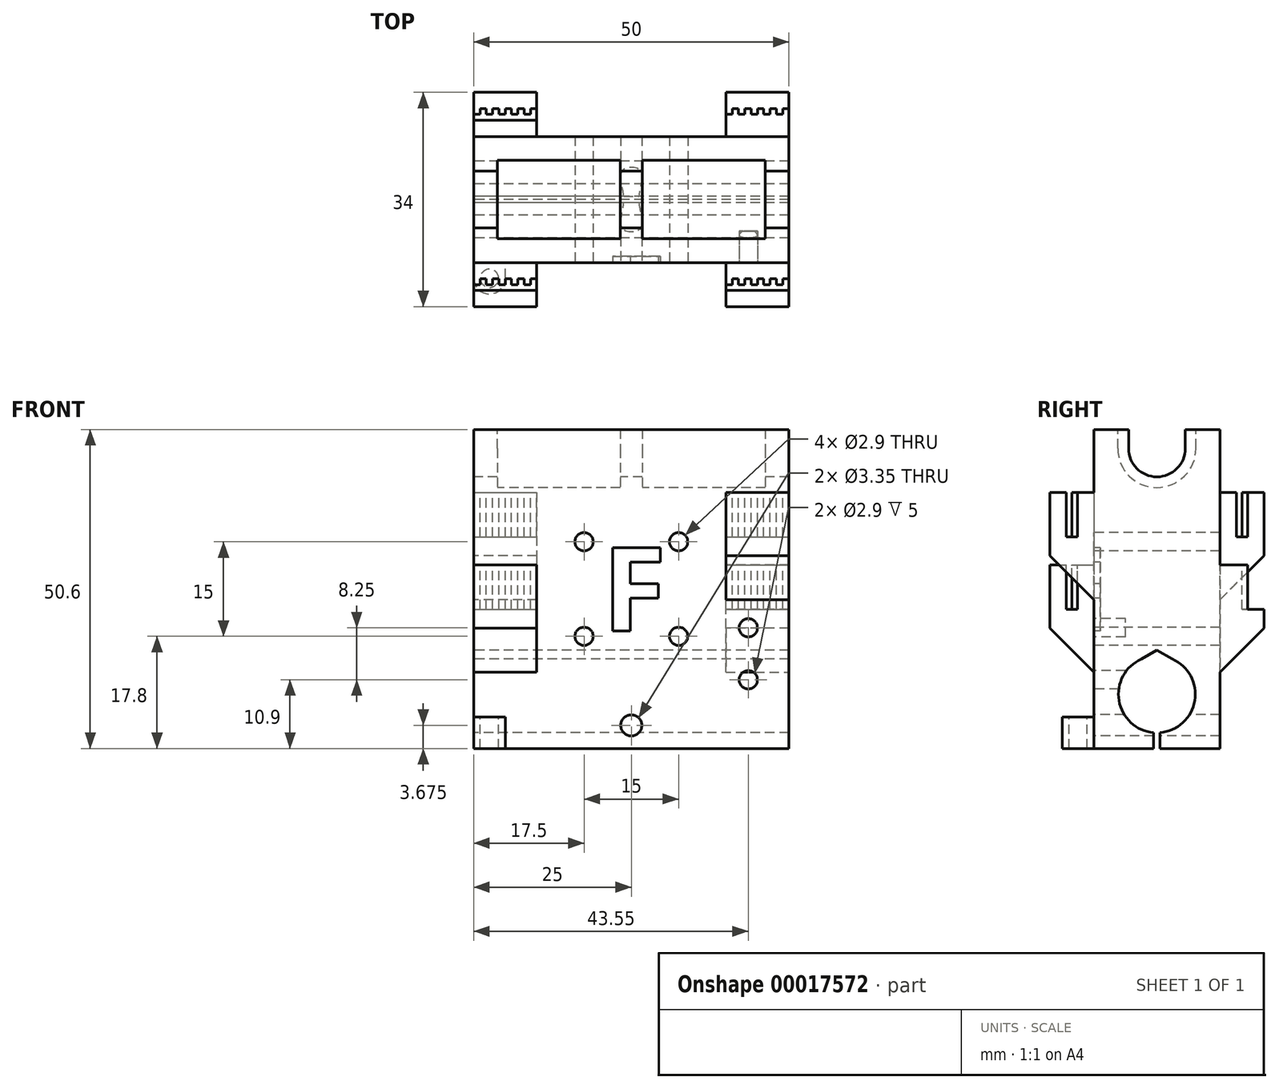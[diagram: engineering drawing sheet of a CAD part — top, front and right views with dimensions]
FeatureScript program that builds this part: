
annotation { "Feature Type Name" : "Feature", "Feature Type Description" : "" }
export const myFeature = defineFeature(function(context is Context, id is Id, definition is map)
    precondition{}
    {
        {
            var Q0;
            Q0=qCreatedBy(makeId("Top.planeOp"),FACE);
            var sketch = newSketch(context, id + "F0", { "sketchPlane" : qUnion([Q0])});
            skLineSegment(sketch, "E0.bottom", {"start": v(0, 0) * mm, "end": v(50, 0) * mm});
            skLineSegment(sketch, "E0.top", {"start": v(0, 20) * mm, "end": v(50, 20) * mm});
            skLineSegment(sketch, "E0.left", {"start": v(0, 0) * mm, "end": v(0, 20) * mm});
            skLineSegment(sketch, "E0.right", {"start": v(50, 0) * mm, "end": v(50, 20) * mm});
            skSolve(sketch);
        }
        {
            var Q0;
            Q0=qSketchRegion(id+"F0",true);
            extrude(context, id + "F1", {"entities" : qUnion([Q0]), "depth" : 50.6 * mm});
        }
        {
            var Q0;
            Q0=makeQuery(id+"F1.opExtrude","SWEPT_FACE",FACE,{"disambiguationData":[OSD([sQuery(id+"F0.wireOp",EDGE,"E0.left")])]});
            var sketch = newSketch(context, id + "F2", { "sketchPlane" : qUnion([Q0])});
            skCircle(sketch, "E1", {"center": v(-10, 8.6) * mm, "radius": 6.1 * mm});
            skCircle(sketch, "E2", {"center": v(-10, 47.6) * mm, "radius": 4.5 * mm});
            skLineSegment(sketch, "E3", {"start": v(-20, 47.6) * mm, "end": v(0, 47.6) * mm, "construction": true});
            skLineSegment(sketch, "E4", {"start": v(-14.5, 50.6) * mm, "end": v(-14.5, 47.6) * mm});
            skLineSegment(sketch, "E5", {"start": v(-5.5, 50.6) * mm, "end": v(-5.5, 47.6) * mm});
            skLineSegment(sketch, "E6", {"start": v(-20, 8.6) * mm, "end": v(0, 8.6) * mm, "construction": true});
            skLineSegment(sketch, "E7", {"start": v(-10, 8.6) * mm, "end": v(-10, 0) * mm, "construction": true});
            skLineSegment(sketch, "E8", {"start": v(-10, 0) * mm, "end": v(-10.5, 0) * mm});
            skLineSegment(sketch, "E9", {"start": v(-10.5, 0) * mm, "end": v(-10.5, 2.52) * mm});
            skLineSegment(sketch, "E10", {"start": v(-10.5, 2.52) * mm, "end": v(-9.5, 2.52) * mm});
            skLineSegment(sketch, "E11", {"start": v(-9.5, 2.52) * mm, "end": v(-9.5, 0) * mm});
            skLineSegment(sketch, "E12", {"start": v(-9.5, 0) * mm, "end": v(-10, 0) * mm});
            skLineSegment(sketch, "E13", {"start": v(-10, 14.7) * mm, "end": v(-10, 15.6) * mm});
            skLineSegment(sketch, "E14", {"start": v(-10, 15.6) * mm, "end": v(-6.39, 13.51) * mm});
            skLineSegment(sketch, "E15", {"start": v(-10, 15.6) * mm, "end": v(-13.61, 13.51) * mm});
            skCircle(sketch, "E16", {"center": v(-10, 47.6) * mm, "radius": 6.2 * mm});
            skLineSegment(sketch, "E17", {"start": v(-3.8, 47.6) * mm, "end": v(-3.8, 50.6) * mm});
            skLineSegment(sketch, "E18", {"start": v(-16.2, 47.6) * mm, "end": v(-16.2, 50.6) * mm});
            skSolve(sketch);
        }
        {
            var Q0;
            {var subQ0=sQuery(id+"F2.wireOp",EDGE,"E14");var subQ1=sQuery(id+"F2.wireOp",EDGE,"E1");var subQ3=makeQuery(id+"F2.imprint","INTERSECT",VERTEX,{"disambiguationData":[OD(0.0)],"derivedFrom":[subQ1,subQ0]});Q0=makeQuery(id+"F2.imprint","IMPRINT",FACE,{"disambiguationData":[TD([[makeQuery(id+"F2.imprint","IMPRINT",EDGE,{"disambiguationData":[TD([[subQ3,-1.0]])],"derivedFrom":subQ1}),1.0]])]});}
            var Q1;
            {var subQ0=sQuery(id+"F2.wireOp",EDGE,"E15");var subQ1=sQuery(id+"F2.wireOp",EDGE,"E1");var subQ3=makeQuery(id+"F2.imprint","INTERSECT",VERTEX,{"disambiguationData":[OD(0.0)],"derivedFrom":[subQ1,subQ0]});Q1=makeQuery(id+"F2.imprint","IMPRINT",FACE,{"disambiguationData":[TD([[makeQuery(id+"F2.imprint","IMPRINT",EDGE,{"disambiguationData":[TD([[subQ3,1.0]])],"derivedFrom":subQ1}),1.0]])]});}
            var Q2;
            Q2=makeQuery(id+"F2.imprint","IMPRINT",FACE,{"disambiguationData":[TD([[makeQuery(id+"F2.imprint","IMPRINT",EDGE,{"derivedFrom":sQuery(id+"F2.wireOp",EDGE,"E8")}),-1.0]])]});
            var Q3;
            {var subQ0=sQuery(id+"F2.wireOp",EDGE,"E10");Q3=makeQuery(id+"F2.imprint","IMPRINT",FACE,{"disambiguationData":[TD([[makeQuery(id+"F2.imprint","IMPRINT",EDGE,{"derivedFrom":subQ0}),-1.0]])]});}
            var Q4;
            {var subQ3=sQuery(id+"F2.wireOp",EDGE,"E13");Q4=makeQuery(id+"F2.imprint","IMPRINT",FACE,{"disambiguationData":[TD([[makeQuery(id+"F2.imprint","IMPRINT",EDGE,{"derivedFrom":subQ3}),-1.0]])]});}
            var Q5;
            {var subQ3=sQuery(id+"F2.wireOp",EDGE,"E13");Q5=makeQuery(id+"F2.imprint","IMPRINT",FACE,{"disambiguationData":[TD([[makeQuery(id+"F2.imprint","IMPRINT",EDGE,{"derivedFrom":subQ3}),1.0]])]});}
            var Q6;
            {var subQ7=sQuery(id+"F2.wireOp",EDGE,"E10");Q6=makeQuery(id+"F2.imprint","IMPRINT",FACE,{"disambiguationData":[TD([[makeQuery(id+"F2.imprint","IMPRINT",EDGE,{"derivedFrom":subQ7}),1.0]])]});}
            var Q7;
            {var subQ3=sQuery(id+"F2.wireOp",EDGE,"E5");Q7=makeQuery(id+"F2.imprint","IMPRINT",FACE,{"disambiguationData":[TD([[makeQuery(id+"F2.imprint","IMPRINT",EDGE,{"derivedFrom":subQ3}),-1.0]])]});}
            var Q8;
            {var subQ0=sQuery(id+"F2.wireOp",EDGE,"E4");Q8=makeQuery(id+"F2.imprint","IMPRINT",FACE,{"disambiguationData":[TD([[makeQuery(id+"F2.imprint","IMPRINT",EDGE,{"derivedFrom":subQ0}),1.0]])]});}
            var Q9;
            {var subQ0=sQuery(id+"F2.wireOp",EDGE,"E4");Q9=makeQuery(id+"F2.imprint","IMPRINT",FACE,{"disambiguationData":[TD([[makeQuery(id+"F2.imprint","IMPRINT",EDGE,{"derivedFrom":subQ0}),1.0]])]});}
            var Q10;
            {var subQ3=sQuery(id+"F2.wireOp",EDGE,"E5");Q10=makeQuery(id+"F2.imprint","IMPRINT",FACE,{"disambiguationData":[TD([[makeQuery(id+"F2.imprint","IMPRINT",EDGE,{"derivedFrom":subQ3}),-1.0]])]});}
            var Q11;
            {var subQ1=sQuery(id+"F2.wireOp",EDGE,"E2");var subQ4=makeQuery(id+"F2.imprint","INTERSECT",VERTEX,{"derivedFrom":[subQ1,sQuery(id+"F2.wireOp",EDGE,"E5")]});Q11=makeQuery(id+"F2.imprint","IMPRINT",FACE,{"disambiguationData":[TD([[makeQuery(id+"F2.imprint","IMPRINT",EDGE,{"disambiguationData":[TD([[subQ4,-1.0]])],"derivedFrom":subQ1}),1.0]])]});}
            extrude(context, id + "F3", {"entities" : qUnion([Q0, Q1, Q2, Q3, Q4, Q5, Q6, Q7, Q8, Q9, Q10, Q11]), "operationType" : NewBodyOperationType.REMOVE, "endBound" : BoundingType.THROUGH_ALL, "oppositeDirection" : true, "depth" : 25 * mm});
        }
        {
            var Q0;
            {var subQ3=sQuery(id+"F2.wireOp",EDGE,"E4");Q0=makeQuery(id+"F2.imprint","IMPRINT",FACE,{"disambiguationData":[TD([[makeQuery(id+"F2.imprint","IMPRINT",EDGE,{"derivedFrom":subQ3}),-1.0]])]});}
            var Q1;
            {var subQ3=sQuery(id+"F2.wireOp",EDGE,"E18");Q1=makeQuery(id+"F2.imprint","IMPRINT",FACE,{"disambiguationData":[TD([[makeQuery(id+"F2.imprint","IMPRINT",EDGE,{"derivedFrom":subQ3}),-1.0]])]});}
            var Q2;
            {var subQ3=sQuery(id+"F2.wireOp",EDGE,"E17");Q2=makeQuery(id+"F2.imprint","IMPRINT",FACE,{"disambiguationData":[TD([[makeQuery(id+"F2.imprint","IMPRINT",EDGE,{"derivedFrom":subQ3}),1.0]])]});}
            extrude(context, id + "F4", {"entities" : qUnion([Q0, Q1, Q2]), "operationType" : NewBodyOperationType.REMOVE, "oppositeDirection" : true, "depth" : 46.25 * mm});
        }
        {
            var Q0;
            {var subQ3=sQuery(id+"F2.wireOp",EDGE,"E4");Q0=makeQuery(id+"F2.imprint","IMPRINT",FACE,{"disambiguationData":[TD([[makeQuery(id+"F2.imprint","IMPRINT",EDGE,{"derivedFrom":subQ3}),-1.0]])]});}
            var Q1;
            {var subQ3=sQuery(id+"F2.wireOp",EDGE,"E18");Q1=makeQuery(id+"F2.imprint","IMPRINT",FACE,{"disambiguationData":[TD([[makeQuery(id+"F2.imprint","IMPRINT",EDGE,{"derivedFrom":subQ3}),-1.0]])]});}
            var Q2;
            {var subQ3=sQuery(id+"F2.wireOp",EDGE,"E17");Q2=makeQuery(id+"F2.imprint","IMPRINT",FACE,{"disambiguationData":[TD([[makeQuery(id+"F2.imprint","IMPRINT",EDGE,{"derivedFrom":subQ3}),1.0]])]});}
            extrude(context, id + "F5", {"entities" : qUnion([Q0, Q1, Q2]), "operationType" : NewBodyOperationType.ADD, "oppositeDirection" : true, "depth" : 26.75 * mm});
        }
        {
            var Q0;
            {var subQ3=sQuery(id+"F2.wireOp",EDGE,"E4");Q0=makeQuery(id+"F2.imprint","IMPRINT",FACE,{"disambiguationData":[TD([[makeQuery(id+"F2.imprint","IMPRINT",EDGE,{"derivedFrom":subQ3}),-1.0]])]});}
            var Q1;
            {var subQ3=sQuery(id+"F2.wireOp",EDGE,"E18");Q1=makeQuery(id+"F2.imprint","IMPRINT",FACE,{"disambiguationData":[TD([[makeQuery(id+"F2.imprint","IMPRINT",EDGE,{"derivedFrom":subQ3}),-1.0]])]});}
            var Q2;
            {var subQ3=sQuery(id+"F2.wireOp",EDGE,"E17");Q2=makeQuery(id+"F2.imprint","IMPRINT",FACE,{"disambiguationData":[TD([[makeQuery(id+"F2.imprint","IMPRINT",EDGE,{"derivedFrom":subQ3}),1.0]])]});}
            extrude(context, id + "F6", {"entities" : qUnion([Q0, Q1, Q2]), "operationType" : NewBodyOperationType.REMOVE, "oppositeDirection" : true, "depth" : 23.25 * mm});
        }
        {
            var Q0;
            {var subQ3=sQuery(id+"F2.wireOp",EDGE,"E4");Q0=makeQuery(id+"F2.imprint","IMPRINT",FACE,{"disambiguationData":[TD([[makeQuery(id+"F2.imprint","IMPRINT",EDGE,{"derivedFrom":subQ3}),-1.0]])]});}
            var Q1;
            {var subQ3=sQuery(id+"F2.wireOp",EDGE,"E18");Q1=makeQuery(id+"F2.imprint","IMPRINT",FACE,{"disambiguationData":[TD([[makeQuery(id+"F2.imprint","IMPRINT",EDGE,{"derivedFrom":subQ3}),-1.0]])]});}
            var Q2;
            {var subQ3=sQuery(id+"F2.wireOp",EDGE,"E17");Q2=makeQuery(id+"F2.imprint","IMPRINT",FACE,{"disambiguationData":[TD([[makeQuery(id+"F2.imprint","IMPRINT",EDGE,{"derivedFrom":subQ3}),1.0]])]});}
            extrude(context, id + "F7", {"entities" : qUnion([Q0, Q1, Q2]), "operationType" : NewBodyOperationType.ADD, "oppositeDirection" : true, "depth" : 3.75 * mm});
        }
        {
            var Q0;
            Q0=makeQuery(id+"F1.opExtrude","SWEPT_FACE",FACE,{"disambiguationData":[OSD([sQuery(id+"F0.wireOp",EDGE,"E0.bottom")])]});
            var sketch = newSketch(context, id + "F8", { "sketchPlane" : qUnion([Q0])});
            skLineSegment(sketch, "E19.bottom", {"start": v(0, 29.1) * mm, "end": v(10, 29.1) * mm});
            skLineSegment(sketch, "E19.top", {"start": v(0, 9.1) * mm, "end": v(10, 9.1) * mm});
            skLineSegment(sketch, "E19.left", {"start": v(0, 29.1) * mm, "end": v(0, 9.1) * mm});
            skLineSegment(sketch, "E19.right", {"start": v(10, 29.1) * mm, "end": v(10, 9.1) * mm});
            skLineSegment(sketch, "E20.bottom", {"start": v(50, 40.6) * mm, "end": v(40, 40.6) * mm});
            skLineSegment(sketch, "E20.top", {"start": v(50, 20.6) * mm, "end": v(40, 20.6) * mm});
            skLineSegment(sketch, "E20.left", {"start": v(50, 40.6) * mm, "end": v(50, 20.6) * mm});
            skLineSegment(sketch, "E20.right", {"start": v(40, 40.6) * mm, "end": v(40, 20.6) * mm});
            skPoint(sketch, "E21", {"position": v(0, 47.6) * mm});
            skPoint(sketch, "E22", {"position": v(0, 8.6) * mm});
            skSolve(sketch);
        }
        {
            var Q0;
            Q0=qSketchRegion(id+"F8",true);
            extrude(context, id + "F9", {"entities" : qUnion([Q0]), "operationType" : NewBodyOperationType.ADD, "depth" : 7 * mm});
        }
        {
            var Q0;
            Q0=makeQuery(id+"F9.opExtrude","CAP_EDGE",EDGE,{"disambiguationData":[OSD([sQuery(id+"F8.wireOp",EDGE,"E19.top")])],"isStart":false});
            var Q1;
            Q1=makeQuery(id+"F9.opExtrude","CAP_EDGE",EDGE,{"disambiguationData":[OSD([sQuery(id+"F8.wireOp",EDGE,"E20.top")])],"isStart":false});
            chamfer(context, id + "F10", {"entities" : qUnion([Q0, Q1]), "width" : 10 * mm, "tangentPropagation" : true});
        }
        {
            var Q0;
            Q0=makeQuery(id+"F9.opExtrude","SWEPT_FACE",FACE,{"disambiguationData":[OSD([sQuery(id+"F8.wireOp",EDGE,"E19.bottom")])]});
            var sketch = newSketch(context, id + "F11", { "sketchPlane" : qUnion([Q0])});
            skLineSegment(sketch, "E23", {"start": v(-935.9, 0) * mm, "end": v(-935.88, -4.54) * mm});
            skLineSegment(sketch, "E24.left", {"start": v(0, -4.4) * mm, "end": v(0, -2.6) * mm});
            skLineSegment(sketch, "E25", {"start": v(6, -3.5) * mm, "end": v(7, -3.5) * mm});
            skLineSegment(sketch, "E26", {"start": v(4, -3.5) * mm, "end": v(5, -3.5) * mm});
            skLineSegment(sketch, "E27", {"start": v(0, -3.5) * mm, "end": v(1, -3.5) * mm});
            skLineSegment(sketch, "E28", {"start": v(7, -2.6) * mm, "end": v(8, -2.6) * mm});
            skLineSegment(sketch, "E29", {"start": v(2, -3.5) * mm, "end": v(3, -3.5) * mm});
            skLineSegment(sketch, "E30", {"start": v(3, -2.6) * mm, "end": v(4, -2.6) * mm});
            skLineSegment(sketch, "E31", {"start": v(8, -3.5) * mm, "end": v(9, -3.5) * mm});
            skLineSegment(sketch, "E32", {"start": v(8, -2.6) * mm, "end": v(8, -3.5) * mm});
            skLineSegment(sketch, "E33", {"start": v(9, -3.5) * mm, "end": v(9, -2.6) * mm});
            skLineSegment(sketch, "E34", {"start": v(10, -2.6) * mm, "end": v(10, -3.5) * mm});
            skLineSegment(sketch, "E35", {"start": v(6, -2.6) * mm, "end": v(6, -3.5) * mm});
            skLineSegment(sketch, "E36", {"start": v(2, -2.6) * mm, "end": v(2, -3.5) * mm});
            skLineSegment(sketch, "E37", {"start": v(1, -2.6) * mm, "end": v(2, -2.6) * mm});
            skLineSegment(sketch, "E38", {"start": v(1, -3.5) * mm, "end": v(1, -2.6) * mm});
            skLineSegment(sketch, "E39", {"start": v(9, -2.6) * mm, "end": v(10, -2.6) * mm});
            skLineSegment(sketch, "E40", {"start": v(5, -2.6) * mm, "end": v(6, -2.6) * mm});
            skLineSegment(sketch, "E41", {"start": v(5, -3.5) * mm, "end": v(5, -2.6) * mm});
            skLineSegment(sketch, "E42", {"start": v(3, -3.5) * mm, "end": v(3, -2.6) * mm});
            skLineSegment(sketch, "E43", {"start": v(4, -2.6) * mm, "end": v(4, -3.5) * mm});
            skLineSegment(sketch, "E44", {"start": v(7, -3.5) * mm, "end": v(7, -2.6) * mm});
            skLineSegment(sketch, "E45", {"start": v(0, -2.6) * mm, "end": v(0, -3.5) * mm});
            skLineSegment(sketch, "E46", {"start": v(10, -3.5) * mm, "end": v(10, -4.4) * mm});
            skLineSegment(sketch, "E47", {"start": v(0, -4.4) * mm, "end": v(10, -4.4) * mm});
            skLineSegment(sketch, "E48", {"start": v(5.3, -2.6) * mm, "end": v(5.3, 0) * mm});
            skSolve(sketch);
        }
        {
            var Q0;
            Q0=qSketchRegion(id+"F11",true);
            extrude(context, id + "F12", {"entities" : qUnion([Q0]), "operationType" : NewBodyOperationType.REMOVE, "oppositeDirection" : true, "depth" : 7 * mm});
        }
        {
            var Q0;
            Q0=makeQuery(id+"F9.opExtrude","SWEPT_FACE",FACE,{"disambiguationData":[OSD([sQuery(id+"F8.wireOp",EDGE,"E20.bottom")])]});
            var sketch = newSketch(context, id + "F13", { "sketchPlane" : qUnion([Q0])});
            skLineSegment(sketch, "E49.left", {"start": v(40, -4.4) * mm, "end": v(40, -2.6) * mm});
            skLineSegment(sketch, "E50", {"start": v(46, -3.5) * mm, "end": v(47, -3.5) * mm});
            skLineSegment(sketch, "E51", {"start": v(44, -3.5) * mm, "end": v(45, -3.5) * mm});
            skLineSegment(sketch, "E52", {"start": v(40, -3.5) * mm, "end": v(41, -3.5) * mm});
            skLineSegment(sketch, "E53", {"start": v(47, -2.6) * mm, "end": v(48, -2.6) * mm});
            skLineSegment(sketch, "E54", {"start": v(42, -3.5) * mm, "end": v(43, -3.5) * mm});
            skLineSegment(sketch, "E55", {"start": v(43, -2.6) * mm, "end": v(44, -2.6) * mm});
            skLineSegment(sketch, "E56", {"start": v(48, -3.5) * mm, "end": v(49, -3.5) * mm});
            skLineSegment(sketch, "E57", {"start": v(48, -2.6) * mm, "end": v(48, -3.5) * mm});
            skLineSegment(sketch, "E58", {"start": v(49, -3.5) * mm, "end": v(49, -2.6) * mm});
            skLineSegment(sketch, "E59", {"start": v(50, -2.6) * mm, "end": v(50, -3.5) * mm});
            skLineSegment(sketch, "E60", {"start": v(46, -2.6) * mm, "end": v(46, -3.5) * mm});
            skLineSegment(sketch, "E61", {"start": v(42, -2.6) * mm, "end": v(42, -3.5) * mm});
            skLineSegment(sketch, "E62", {"start": v(41, -2.6) * mm, "end": v(42, -2.6) * mm});
            skLineSegment(sketch, "E63", {"start": v(41, -3.5) * mm, "end": v(41, -2.6) * mm});
            skLineSegment(sketch, "E64", {"start": v(49, -2.6) * mm, "end": v(50, -2.6) * mm});
            skLineSegment(sketch, "E65", {"start": v(45, -2.6) * mm, "end": v(46, -2.6) * mm});
            skLineSegment(sketch, "E66", {"start": v(45, -3.5) * mm, "end": v(45, -2.6) * mm});
            skLineSegment(sketch, "E67", {"start": v(43, -3.5) * mm, "end": v(43, -2.6) * mm});
            skLineSegment(sketch, "E68", {"start": v(44, -2.6) * mm, "end": v(44, -3.5) * mm});
            skLineSegment(sketch, "E69", {"start": v(47, -3.5) * mm, "end": v(47, -2.6) * mm});
            skLineSegment(sketch, "E70", {"start": v(40, -2.6) * mm, "end": v(40, -3.5) * mm});
            skLineSegment(sketch, "E71", {"start": v(50, -3.5) * mm, "end": v(50, -4.4) * mm});
            skLineSegment(sketch, "E72", {"start": v(40, -4.4) * mm, "end": v(50, -4.4) * mm});
            skLineSegment(sketch, "E73", {"start": v(45.23, -2.6) * mm, "end": v(45.23, 0) * mm});
            skSolve(sketch);
        }
        {
            var Q0;
            Q0=qSketchRegion(id+"F13",true);
            extrude(context, id + "F14", {"entities" : qUnion([Q0]), "operationType" : NewBodyOperationType.REMOVE, "oppositeDirection" : true, "depth" : 7 * mm});
        }
        {
            var Q0;
            Q0=makeQuery(id+"F1.opExtrude","SWEPT_FACE",FACE,{"disambiguationData":[OSD([sQuery(id+"F0.wireOp",EDGE,"E0.top")])]});
            var sketch = newSketch(context, id + "F15", { "sketchPlane" : qUnion([Q0])});
            skLineSegment(sketch, "E74.bottom", {"start": v(-50, 9.1) * mm, "end": v(-40, 9.1) * mm});
            skLineSegment(sketch, "E74.top", {"start": v(-50, 29.1) * mm, "end": v(-40, 29.1) * mm});
            skLineSegment(sketch, "E74.left", {"start": v(-50, 9.1) * mm, "end": v(-50, 29.1) * mm});
            skLineSegment(sketch, "E74.right", {"start": v(-40, 9.1) * mm, "end": v(-40, 29.1) * mm});
            skLineSegment(sketch, "E75.bottom", {"start": v(0, 40.6) * mm, "end": v(-10, 40.6) * mm});
            skLineSegment(sketch, "E75.top", {"start": v(0, 20.6) * mm, "end": v(-10, 20.6) * mm});
            skLineSegment(sketch, "E75.left", {"start": v(0, 40.6) * mm, "end": v(0, 20.6) * mm});
            skLineSegment(sketch, "E75.right", {"start": v(-10, 40.6) * mm, "end": v(-10, 20.6) * mm});
            skSolve(sketch);
        }
        {
            var Q0;
            Q0=qSketchRegion(id+"F15",true);
            extrude(context, id + "F16", {"entities" : qUnion([Q0]), "operationType" : NewBodyOperationType.ADD, "depth" : 7 * mm});
        }
        {
            var Q0;
            Q0=makeQuery(id+"F16.opExtrude","SWEPT_FACE",FACE,{"disambiguationData":[OSD([sQuery(id+"F15.wireOp",EDGE,"E74.top")])]});
            var sketch = newSketch(context, id + "F17", { "sketchPlane" : qUnion([Q0])});
            skLineSegment(sketch, "E76.left", {"start": v(40, 22.6) * mm, "end": v(40, 24.4) * mm});
            skLineSegment(sketch, "E77", {"start": v(46, 23.5) * mm, "end": v(47, 23.5) * mm});
            skLineSegment(sketch, "E78", {"start": v(44, 23.5) * mm, "end": v(45, 23.5) * mm});
            skLineSegment(sketch, "E79", {"start": v(40, 23.5) * mm, "end": v(41, 23.5) * mm});
            skLineSegment(sketch, "E80", {"start": v(47, 24.4) * mm, "end": v(48, 24.4) * mm});
            skLineSegment(sketch, "E81", {"start": v(42, 23.5) * mm, "end": v(43, 23.5) * mm});
            skLineSegment(sketch, "E82", {"start": v(43, 24.4) * mm, "end": v(44, 24.4) * mm});
            skLineSegment(sketch, "E83", {"start": v(48, 23.5) * mm, "end": v(49, 23.5) * mm});
            skLineSegment(sketch, "E84", {"start": v(48, 24.4) * mm, "end": v(48, 23.5) * mm});
            skLineSegment(sketch, "E85", {"start": v(49, 23.5) * mm, "end": v(49, 24.4) * mm});
            skLineSegment(sketch, "E86", {"start": v(50, 24.4) * mm, "end": v(50, 23.5) * mm});
            skLineSegment(sketch, "E87", {"start": v(46, 24.4) * mm, "end": v(46, 23.5) * mm});
            skLineSegment(sketch, "E88", {"start": v(42, 24.4) * mm, "end": v(42, 23.5) * mm});
            skLineSegment(sketch, "E89", {"start": v(41, 24.4) * mm, "end": v(42, 24.4) * mm});
            skLineSegment(sketch, "E90", {"start": v(41, 23.5) * mm, "end": v(41, 24.4) * mm});
            skLineSegment(sketch, "E91", {"start": v(49, 24.4) * mm, "end": v(50, 24.4) * mm});
            skLineSegment(sketch, "E92", {"start": v(45, 24.4) * mm, "end": v(46, 24.4) * mm});
            skLineSegment(sketch, "E93", {"start": v(45, 23.5) * mm, "end": v(45, 24.4) * mm});
            skLineSegment(sketch, "E94", {"start": v(43, 23.5) * mm, "end": v(43, 24.4) * mm});
            skLineSegment(sketch, "E95", {"start": v(44, 24.4) * mm, "end": v(44, 23.5) * mm});
            skLineSegment(sketch, "E96", {"start": v(47, 23.5) * mm, "end": v(47, 24.4) * mm});
            skLineSegment(sketch, "E97", {"start": v(40, 24.4) * mm, "end": v(40, 23.5) * mm});
            skLineSegment(sketch, "E98", {"start": v(50, 23.5) * mm, "end": v(50, 22.6) * mm});
            skLineSegment(sketch, "E99", {"start": v(40, 22.6) * mm, "end": v(50, 22.6) * mm});
            skLineSegment(sketch, "E100", {"start": v(45, 22.6) * mm, "end": v(45, 20) * mm});
            skSolve(sketch);
        }
        {
            var Q0;
            {var subQ4=sQuery(id+"F17.wireOp",EDGE,"E76.left");Q0=makeQuery(id+"F17.imprint","IMPRINT",FACE,{"disambiguationData":[TD([[makeQuery(id+"F17.imprint","IMPRINT",EDGE,{"derivedFrom":subQ4}),1.0]])]});}
            extrude(context, id + "F18", {"entities" : qUnion([Q0]), "operationType" : NewBodyOperationType.REMOVE, "oppositeDirection" : true, "depth" : 7 * mm});
        }
        {
            var Q0;
            Q0=makeQuery(id+"F16.opExtrude","SWEPT_FACE",FACE,{"disambiguationData":[OSD([sQuery(id+"F15.wireOp",EDGE,"E75.bottom")])]});
            var sketch = newSketch(context, id + "F19", { "sketchPlane" : qUnion([Q0])});
            skLineSegment(sketch, "E101", {"start": v(6, 23.5) * mm, "end": v(7, 23.5) * mm});
            skLineSegment(sketch, "E102", {"start": v(4, 23.5) * mm, "end": v(5, 23.5) * mm});
            skLineSegment(sketch, "E103", {"start": v(0, 23.5) * mm, "end": v(1, 23.5) * mm});
            skLineSegment(sketch, "E104", {"start": v(7, 24.4) * mm, "end": v(8, 24.4) * mm});
            skLineSegment(sketch, "E105", {"start": v(2, 23.5) * mm, "end": v(3, 23.5) * mm});
            skLineSegment(sketch, "E106", {"start": v(3, 24.4) * mm, "end": v(4, 24.4) * mm});
            skLineSegment(sketch, "E107", {"start": v(8, 23.5) * mm, "end": v(9, 23.5) * mm});
            skLineSegment(sketch, "E108", {"start": v(8, 24.4) * mm, "end": v(8, 23.5) * mm});
            skLineSegment(sketch, "E109", {"start": v(9, 23.5) * mm, "end": v(9, 24.4) * mm});
            skLineSegment(sketch, "E110", {"start": v(10, 24.4) * mm, "end": v(10, 23.5) * mm});
            skLineSegment(sketch, "E111", {"start": v(6, 24.4) * mm, "end": v(6, 23.5) * mm});
            skLineSegment(sketch, "E112", {"start": v(2, 24.4) * mm, "end": v(2, 23.5) * mm});
            skLineSegment(sketch, "E113", {"start": v(1, 24.4) * mm, "end": v(2, 24.4) * mm});
            skLineSegment(sketch, "E114", {"start": v(1, 23.5) * mm, "end": v(1, 24.4) * mm});
            skLineSegment(sketch, "E115", {"start": v(9, 24.4) * mm, "end": v(10, 24.4) * mm});
            skLineSegment(sketch, "E116", {"start": v(5, 24.4) * mm, "end": v(6, 24.4) * mm});
            skLineSegment(sketch, "E117", {"start": v(5, 23.5) * mm, "end": v(5, 24.4) * mm});
            skLineSegment(sketch, "E118", {"start": v(3, 23.5) * mm, "end": v(3, 24.4) * mm});
            skLineSegment(sketch, "E119", {"start": v(4, 24.4) * mm, "end": v(4, 23.5) * mm});
            skLineSegment(sketch, "E120", {"start": v(7, 23.5) * mm, "end": v(7, 24.4) * mm});
            skLineSegment(sketch, "E121", {"start": v(10, 23.5) * mm, "end": v(10, 22.6) * mm});
            skLineSegment(sketch, "E122", {"start": v(0, 22.6) * mm, "end": v(10, 22.6) * mm});
            skLineSegment(sketch, "E123", {"start": v(5, 22.6) * mm, "end": v(5, 20) * mm});
            skLineSegment(sketch, "E124", {"start": v(0, 22.6) * mm, "end": v(0, 23.5) * mm});
            skSolve(sketch);
        }
        {
            var Q0;
            Q0=makeQuery(id+"F19.imprint","IMPRINT",FACE,{"disambiguationData":[TD([[makeQuery(id+"F19.imprint","IMPRINT",EDGE,{"derivedFrom":sQuery(id+"F19.wireOp",EDGE,"E101")}),-1.0]])]});
            extrude(context, id + "F20", {"entities" : qUnion([Q0]), "operationType" : NewBodyOperationType.REMOVE, "oppositeDirection" : true, "depth" : 7 * mm});
        }
        {
            var Q0;
            Q0=makeQuery(id+"F16.opExtrude","CAP_EDGE",EDGE,{"disambiguationData":[OSD([sQuery(id+"F15.wireOp",EDGE,"E75.top")])],"isStart":false});
            var Q1;
            Q1=makeQuery(id+"F16.opExtrude","CAP_EDGE",EDGE,{"disambiguationData":[OSD([sQuery(id+"F15.wireOp",EDGE,"E74.bottom")])],"isStart":false});
            chamfer(context, id + "F21", {"entities" : qUnion([Q0, Q1]), "width" : 10 * mm, "tangentPropagation" : true});
        }
        {
            var Q0;
            Q0=makeQuery(id+"F1.opExtrude","SWEPT_FACE",FACE,{"disambiguationData":[OSD([sQuery(id+"F0.wireOp",EDGE,"E0.bottom")])]});
            var sketch = newSketch(context, id + "F22", { "sketchPlane" : qUnion([Q0])});
            skCircle(sketch, "E125", {"center": v(17.5, 32.8) * mm, "radius": 1.45 * mm});
            skCircle(sketch, "E126", {"center": v(32.5, 32.8) * mm, "radius": 1.45 * mm});
            skCircle(sketch, "E127", {"center": v(17.5, 17.8) * mm, "radius": 1.45 * mm});
            skCircle(sketch, "E128", {"center": v(32.5, 17.8) * mm, "radius": 1.45 * mm});
            skLineSegment(sketch, "E129", {"start": v(17.5, 32.8) * mm, "end": v(0, 32.8) * mm});
            skLineSegment(sketch, "E130", {"start": v(32.5, 17.8) * mm, "end": v(50, 17.8) * mm});
            skLineSegment(sketch, "E131", {"start": v(32.5, 32.8) * mm, "end": v(32.5, 50.6) * mm});
            skLineSegment(sketch, "E132", {"start": v(17.5, 17.8) * mm, "end": v(17.5, 0) * mm});
            skCircle(sketch, "E133", {"center": v(25, 3.68) * mm, "radius": 1.68 * mm});
            skLineSegment(sketch, "E134", {"start": v(25, 0) * mm, "end": v(25, 13.82) * mm, "construction": true});
            skSolve(sketch);
        }
        {
            var Q0;
            Q0=qSketchRegion(id+"F22",true);
            var Q1;
            Q1=makeQuery(id+"F22.imprint","IMPRINT",FACE,{"disambiguationData":[TD([[makeQuery(id+"F22.imprint","IMPRINT",EDGE,{"derivedFrom":sQuery(id+"F22.wireOp",EDGE,"E125")}),1.0]])]});
            var Q2;
            Q2=makeQuery(id+"F22.imprint","IMPRINT",FACE,{"disambiguationData":[TD([[makeQuery(id+"F22.imprint","IMPRINT",EDGE,{"derivedFrom":sQuery(id+"F22.wireOp",EDGE,"E126")}),1.0]])]});
            var Q3;
            Q3=makeQuery(id+"F22.imprint","IMPRINT",FACE,{"disambiguationData":[TD([[makeQuery(id+"F22.imprint","IMPRINT",EDGE,{"derivedFrom":sQuery(id+"F22.wireOp",EDGE,"E128")}),1.0]])]});
            var Q4;
            Q4=makeQuery(id+"F22.imprint","IMPRINT",FACE,{"disambiguationData":[TD([[makeQuery(id+"F22.imprint","IMPRINT",EDGE,{"derivedFrom":sQuery(id+"F22.wireOp",EDGE,"E127")}),1.0]])]});
            extrude(context, id + "F23", {"entities" : qUnion([Q0, Q1, Q2, Q3, Q4]), "operationType" : NewBodyOperationType.REMOVE, "endBound" : BoundingType.THROUGH_ALL, "oppositeDirection" : true, "depth" : 25 * mm});
        }
        {
            var Q0;
            Q0=makeQuery(id+"F1.opExtrude","SWEPT_FACE",FACE,{"disambiguationData":[OSD([sQuery(id+"F0.wireOp",EDGE,"E0.bottom")])]});
            var sketch = newSketch(context, id + "F24", { "sketchPlane" : qUnion([Q0])});
            skCircle(sketch, "E135", {"center": v(43.55, 19.15) * mm, "radius": 1.45 * mm});
            skCircle(sketch, "E136", {"center": v(43.55, 10.9) * mm, "radius": 1.45 * mm});
            skSolve(sketch);
        }
        {
            var Q0;
            Q0=qSketchRegion(id+"F24",true);
            extrude(context, id + "F25", {"entities" : qUnion([Q0]), "operationType" : NewBodyOperationType.REMOVE, "oppositeDirection" : true, "depth" : 5 * mm});
        }
        {
            var Q0;
            Q0=makeQuery(id+"F1.opExtrude","SWEPT_FACE",FACE,{"disambiguationData":[OSD([sQuery(id+"F0.wireOp",EDGE,"E0.bottom")])]});
            var sketch = newSketch(context, id + "F26", { "sketchPlane" : qUnion([Q0])});
            skText(sketch, "E137", { "text": "F", "fontName": "OpenSans-Bold.ttf"});
            skLineSegment(sketch, "E138", {"start": v(17.5, 32.8) * mm, "end": v(17.5, 17.8) * mm, "construction": true});
            skLineSegment(sketch, "E139", {"start": v(17.5, 17.8) * mm, "end": v(32.5, 17.8) * mm, "construction": true});
            skLineSegment(sketch, "E140", {"start": v(32.5, 17.8) * mm, "end": v(32.5, 32.8) * mm, "construction": true});
            skLineSegment(sketch, "E141", {"start": v(32.5, 32.8) * mm, "end": v(17.5, 32.8) * mm, "construction": true});
            skLineSegment(sketch, "E142", {"start": v(17.5, 25.3) * mm, "end": v(20.4, 25.3) * mm, "construction": true});
            skLineSegment(sketch, "E143", {"start": v(29.6, 25.3) * mm, "end": v(32.5, 25.3) * mm, "construction": true});
            skLineSegment(sketch, "E144", {"start": v(25, 18.66) * mm, "end": v(25, 17.8) * mm, "construction": true});
            skLineSegment(sketch, "E145", {"start": v(25, 32.8) * mm, "end": v(25, 31.94) * mm, "construction": true});
            const initialGuessF26  = {"E137": [0.0204, 0.01866, 1, 0, 0.01328]};
            skSetInitialGuess(sketch, initialGuessF26);
            skSolve(sketch);
        }
        {
            var Q0;
            Q0=qSketchRegion(id+"F26",true);
            extrude(context, id + "F27", {"entities" : qUnion([Q0]), "operationType" : NewBodyOperationType.REMOVE, "oppositeDirection" : true, "depth" : 1 * mm});
        }
        {
            var Q0;
            Q0=makeQuery(id+"F1.opExtrude","SWEPT_FACE",FACE,{"disambiguationData":[OSD([sQuery(id+"F0.wireOp",EDGE,"E0.bottom")])]});
            var sketch = newSketch(context, id + "F28", { "sketchPlane" : qUnion([Q0])});
            skLineSegment(sketch, "E146.bottom", {"start": v(0, 0) * mm, "end": v(5, 0) * mm});
            skLineSegment(sketch, "E146.top", {"start": v(0, 5) * mm, "end": v(5, 5) * mm});
            skLineSegment(sketch, "E146.left", {"start": v(0, 0) * mm, "end": v(0, 5) * mm});
            skLineSegment(sketch, "E146.right", {"start": v(5, 0) * mm, "end": v(5, 5) * mm});
            skSolve(sketch);
        }
        {
            var Q0;
            Q0=qSketchRegion(id+"F28",true);
            extrude(context, id + "F29", {"entities" : qUnion([Q0]), "operationType" : NewBodyOperationType.ADD, "depth" : 5 * mm});
        }
        {
            var Q0;
            Q0=makeQuery(id+"F29.opExtrude","SWEPT_FACE",FACE,{"disambiguationData":[OSD([sQuery(id+"F28.wireOp",EDGE,"E146.top")])]});
            var sketch = newSketch(context, id + "F30", { "sketchPlane" : qUnion([Q0])});
            skCircle(sketch, "E147", {"center": v(2.5, -2.5) * mm, "radius": 1.45 * mm});
            skLineSegment(sketch, "E148", {"start": v(0, -2.5) * mm, "end": v(5, -2.5) * mm});
            skSolve(sketch);
        }
        {
            var Q0;
            Q0=qSketchRegion(id+"F30",true);
            extrude(context, id + "F31", {"entities" : qUnion([Q0]), "operationType" : NewBodyOperationType.REMOVE, "oppositeDirection" : true, "depth" : 25 * mm});
        }
        {
            var Q0;
            Q0=makeQuery(id+"F29.opExtrude","CAP_EDGE",EDGE,{"disambiguationData":[OSD([sQuery(id+"F28.wireOp",EDGE,"E146.left")])],"isStart":false});
            var Q1;
            Q1=makeQuery(id+"F29.opExtrude","CAP_EDGE",EDGE,{"disambiguationData":[OSD([sQuery(id+"F28.wireOp",EDGE,"E146.right")])],"isStart":false});
            fillet(context, id + "F32", {"entities" : qUnion([Q0, Q1]), "radius" : 2.5 * mm, "tangentPropagation" : true, "allowEdgeOverflow" : false});
        }
    });
